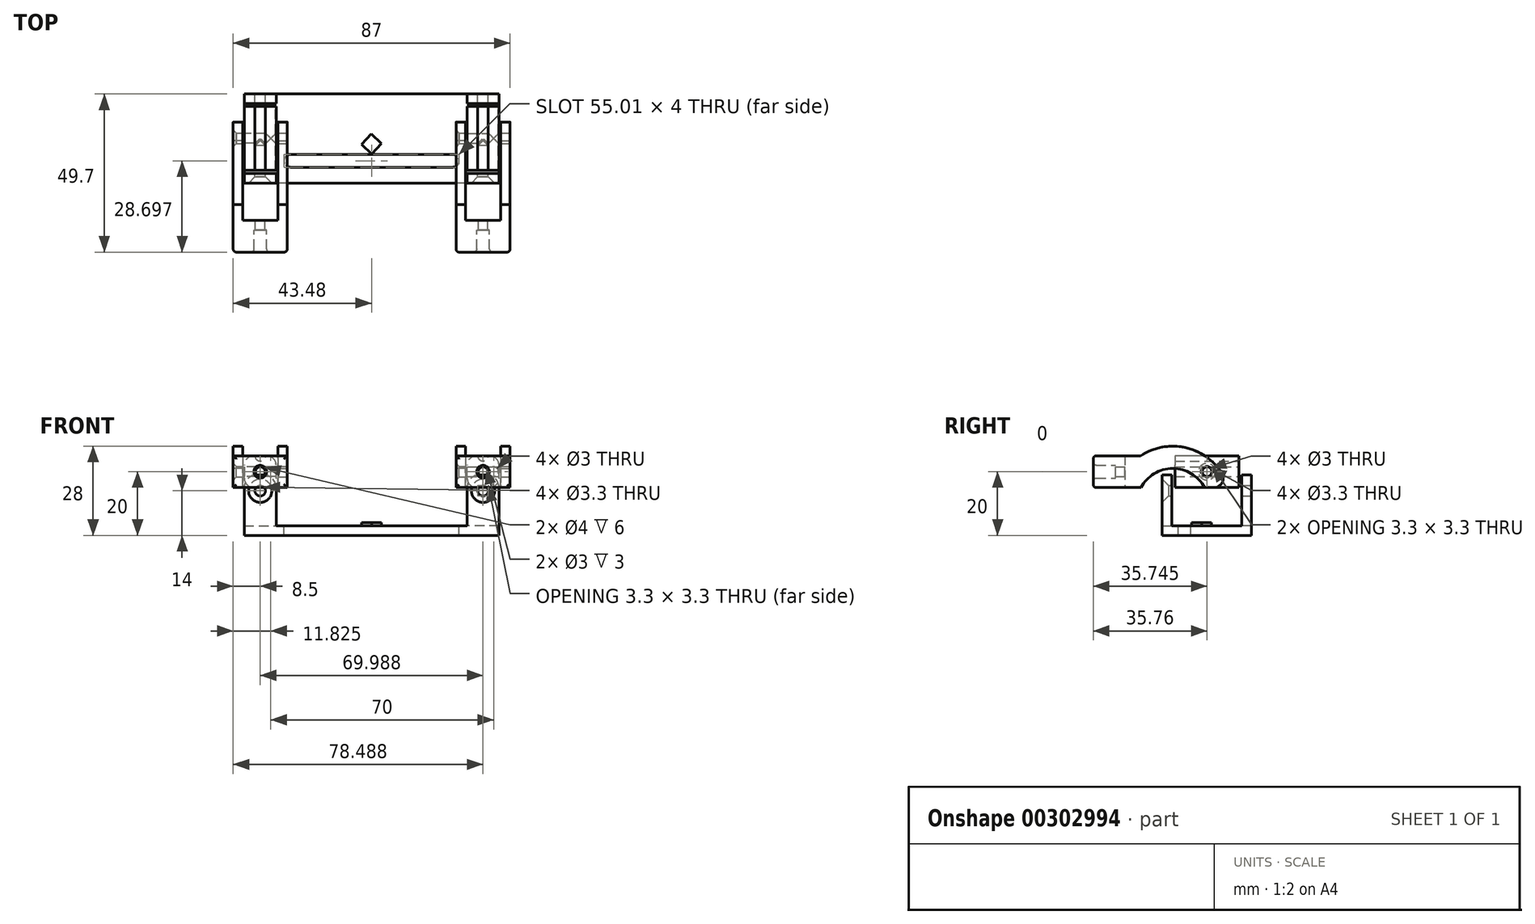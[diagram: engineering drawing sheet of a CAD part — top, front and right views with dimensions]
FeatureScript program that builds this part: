
annotation { "Feature Type Name" : "Feature", "Feature Type Description" : "" }
export const myFeature = defineFeature(function(context is Context, id is Id, definition is map)
    precondition{}
    {
        {
            var Q0;
            Q0=qCreatedBy(makeId("Front.planeOp"),FACE);
            var sketch = newSketch(context, id + "F0", { "sketchPlane" : qUnion([Q0])});
            skCircle(sketch, "E0", {"center": v(0, 0) * mm, "radius": 2 * mm});
            skCircle(sketch, "E1", {"center": v(0, 0) * mm, "radius": 1.5 * mm});
            skCircle(sketch, "E2", {"center": v(0, 0) * mm, "radius": 3.5 * mm});
            skLineSegment(sketch, "E3.bottom", {"start": v(8.5, 5) * mm, "end": v(-8.5, 5) * mm});
            skLineSegment(sketch, "E3.top", {"start": v(8.5, -5) * mm, "end": v(-8.5, -5) * mm});
            skLineSegment(sketch, "E3.left", {"start": v(8.5, 5) * mm, "end": v(8.5, -5) * mm});
            skLineSegment(sketch, "E3.right", {"start": v(-8.5, 5) * mm, "end": v(-8.5, -5) * mm});
            skSolve(sketch);
        }
        {
            var Q0;
            Q0=makeQuery(id+"F0.imprint","IMPRINT",FACE,{"disambiguationData":[TD([[makeQuery(id+"F0.imprint","IMPRINT",EDGE,{"derivedFrom":sQuery(id+"F0.wireOp",EDGE,"E0")}),-1.0]])]});
            extrude(context, id + "F1", {"entities" : qUnion([Q0]), "depth" : 10 * mm});
        }
        {
            var Q0;
            Q0=makeQuery(id+"F0.imprint","IMPRINT",FACE,{"disambiguationData":[TD([[makeQuery(id+"F0.imprint","IMPRINT",EDGE,{"derivedFrom":sQuery(id+"F0.wireOp",EDGE,"E2")}),-1.0]])]});
            extrude(context, id + "F2", {"entities" : qUnion([Q0]), "operationType" : NewBodyOperationType.ADD, "depth" : 10 * mm});
        }
        {
            var Q0;
            Q0=makeQuery(id+"F0.imprint","IMPRINT",FACE,{"disambiguationData":[TD([[makeQuery(id+"F0.imprint","IMPRINT",EDGE,{"derivedFrom":sQuery(id+"F0.wireOp",EDGE,"E0")}),1.0]])]});
            extrude(context, id + "F3", {"entities" : qUnion([Q0]), "operationType" : NewBodyOperationType.ADD, "depth" : 3 * mm});
        }
        {
            var Q0;
            {var subQ5=sQuery(id+"F0.wireOp",EDGE,"E3.left");Q0=makeQuery(id+"F0.imprint","IMPRINT",FACE,{"disambiguationData":[TD([[makeQuery(id+"F0.imprint","IMPRINT",EDGE,{"derivedFrom":subQ5}),-1.0]])]});}
            var sketch = newSketch(context, id + "F4", { "sketchPlane" : qUnion([Q0])});
            skLineSegment(sketch, "E4.bottom", {"start": v(8.5, 5) * mm, "end": v(5.5, 5) * mm});
            skLineSegment(sketch, "E4.top", {"start": v(8.5, -5) * mm, "end": v(5.5, -5) * mm});
            skLineSegment(sketch, "E4.left", {"start": v(8.5, 5) * mm, "end": v(8.5, -5) * mm});
            skLineSegment(sketch, "E4.right", {"start": v(5.5, 5) * mm, "end": v(5.5, -5) * mm});
            skSolve(sketch);
        }
        {
            var Q0;
            {var subQ1=sQuery(id+"F4.wireOp",EDGE,"E4.bottom");Q0=makeQuery(id+"F4.imprint","IMPRINT",FACE,{"disambiguationData":[TD([[makeQuery(id+"F4.imprint","IMPRINT",EDGE,{"derivedFrom":subQ1}),1.0]])]});}
            var Q1;
            {var subQ0=sQuery(id+"F4.wireOp",EDGE,"E4.right");var subQ1=sQuery(id+"F0.wireOp",EDGE,"E2");var subQ2=makeQuery(id+"F0.imprint","IMPRINT",EDGE,{"disambiguationData":[TD([[makeQuery(id+"F0.imprint","INTERSECT",VERTEX,{"derivedFrom":[subQ1,sQuery(id+"F0.wireOp",EDGE,"E3.bottom")]}),1.0]])],"derivedFrom":subQ1});var subQ3=makeQuery(id+"F4.imprint","INTERSECT",VERTEX,{"disambiguationData":[OD(0.0)],"derivedFrom":[subQ2,subQ0]});Q1=makeQuery(id+"F4.imprint","IMPRINT",FACE,{"disambiguationData":[TD([[makeQuery(id+"F4.imprint","IMPRINT",EDGE,{"disambiguationData":[TD([[subQ3,-1.0]])],"derivedFrom":subQ0}),1.0]])]});}
            extrude(context, id + "F5", {"entities" : qUnion([Q0, Q1]), "operationType" : NewBodyOperationType.ADD, "oppositeDirection" : true, "depth" : 5 * mm});
        }
        {
            var Q0;
            {var subQ0=sQuery(id+"F0.wireOp",EDGE,"E0");var subQ1=sQuery(id+"F0.wireOp",EDGE,"E3.top");var subQ2=sQuery(id+"F0.wireOp",EDGE,"E3.bottom");var subQ3=sQuery(id+"F0.wireOp",EDGE,"E2");Q0=makeQuery(id+"F3.boolean.opBoolean","MERGE",FACE,{"derivedFrom":[makeQuery(id+"F2.boolean.opBoolean","MERGE",FACE,{"derivedFrom":[makeQuery(id+"F1.opExtrude","CAP_FACE",FACE,{"disambiguationData":[OSD([subQ0,subQ3])],"isStart":true}),makeQuery(id+"F2.opExtrude","CAP_FACE",FACE,{"disambiguationData":[OSD([subQ3,subQ2,subQ1,sQuery(id+"F0.wireOp",EDGE,"E3.right")])],"isStart":true}),makeQuery(id+"F2.opExtrude","CAP_FACE",FACE,{"disambiguationData":[OSD([subQ3,subQ2,subQ1,sQuery(id+"F0.wireOp",EDGE,"E3.left")])],"isStart":true})]}),makeQuery(id+"F3.opExtrude","CAP_FACE",FACE,{"disambiguationData":[OSD([subQ0,sQuery(id+"F0.wireOp",EDGE,"E1")])],"isStart":true})]});}
            var sketch = newSketch(context, id + "F6", { "sketchPlane" : qUnion([Q0])});
            skLineSegment(sketch, "E5.bottom", {"start": v(8.5, 5) * mm, "end": v(5.5, 5) * mm});
            skLineSegment(sketch, "E5.top", {"start": v(8.5, -5) * mm, "end": v(5.5, -5) * mm});
            skLineSegment(sketch, "E5.left", {"start": v(8.5, 5) * mm, "end": v(8.5, -5) * mm});
            skLineSegment(sketch, "E5.right", {"start": v(5.5, 5) * mm, "end": v(5.5, -5) * mm});
            skSolve(sketch);
        }
        {
            var Q0;
            Q0=makeQuery(id+"F6.imprint","IMPRINT",FACE,{"disambiguationData":[TD([[makeQuery(id+"F6.imprint","IMPRINT",EDGE,{"derivedFrom":sQuery(id+"F6.wireOp",EDGE,"E5.bottom")}),-1.0]])]});
            extrude(context, id + "F7", {"entities" : qUnion([Q0]), "operationType" : NewBodyOperationType.ADD, "depth" : 5 * mm});
        }
        {
            var Q0;
            Q0=makeQuery(id+"F7.boolean.opBoolean","MERGE",FACE,{"derivedFrom":[makeQuery(id+"F2.opExtrude","SWEPT_FACE",FACE,{"disambiguationData":[OSD([sQuery(id+"F0.wireOp",EDGE,"E3.right")])]}),makeQuery(id+"F7.opExtrude","SWEPT_FACE",FACE,{"disambiguationData":[OSD([sQuery(id+"F6.wireOp",EDGE,"E5.left")])]})]});
            var sketch = newSketch(context, id + "F8", { "sketchPlane" : qUnion([Q0])});
            skLineSegment(sketch, "E6", {"start": v(0, 0) * mm, "end": v(-25.94, 0) * mm, "construction": true});
            skPoint(sketch, "E6.endSnap0", {"position": v(-5, 0) * mm});
            skLineSegment(sketch, "E7", {"start": v(0, -5) * mm, "end": v(0, 1) * mm, "construction": true});
            skLineSegment(sketch, "E8", {"start": v(0, 1) * mm, "end": v(-15, 1) * mm, "construction": true});
            skLineSegment(sketch, "E9", {"start": v(0, -5) * mm, "end": v(-25, -5) * mm, "construction": true});
            skArc(sketch, "E10", {"start": v(-15, 1) * mm, "mid": v(-20.83, -0.62) * mm, "end": v(-25, -5) * mm});
            skArc(sketch, "E11", {"start": v(-5, -5) * mm, "mid": v(-9.17, -0.62) * mm, "end": v(-15, 1) * mm});
            skArc(sketch, "E12.0", {"start": v(-15, 8) * mm, "mid": v(-25.92, 4.4) * mm, "end": v(-32.54, -5) * mm});
            skArc(sketch, "E12.1", {"start": v(-4.95, 5) * mm, "mid": v(-9.76, 7.23) * mm, "end": v(-15, 8) * mm});
            skLineSegment(sketch, "E13", {"start": v(-25, -5) * mm, "end": v(-33.46, -5) * mm, "construction": true});
            skLineSegment(sketch, "E14", {"start": v(-32.54, -5) * mm, "end": v(-25, -5) * mm});
            skSolve(sketch);
        }
        {
            var Q0;
            Q0=makeQuery(id+"F8.imprint","IMPRINT",FACE,{"disambiguationData":[TD([[makeQuery(id+"F8.imprint","IMPRINT",EDGE,{"derivedFrom":sQuery(id+"F8.wireOp",EDGE,"E10")}),-1.0]])]});
            extrude(context, id + "F9", {"entities" : qUnion([Q0]), "operationType" : NewBodyOperationType.ADD, "oppositeDirection" : true, "depth" : 3 * mm});
        }
        {
            var Q0;
            Q0=makeQuery(id+"F5.boolean.opBoolean","MERGE",FACE,{"derivedFrom":[makeQuery(id+"F2.opExtrude","SWEPT_FACE",FACE,{"disambiguationData":[OSD([sQuery(id+"F0.wireOp",EDGE,"E3.left")])]}),makeQuery(id+"F5.opExtrude","SWEPT_FACE",FACE,{"disambiguationData":[OSD([sQuery(id+"F4.wireOp",EDGE,"E4.left")])]})]});
            var sketch = newSketch(context, id + "F10", { "sketchPlane" : qUnion([Q0])});
            skLineSegment(sketch, "E15", {"start": v(0, 0) * mm, "end": v(0, -5.22) * mm, "construction": true});
            skLineSegment(sketch, "E16", {"start": v(0, -5) * mm, "end": v(25, -5) * mm, "construction": true});
            skLineSegment(sketch, "E17", {"start": v(0, 1) * mm, "end": v(15, 1) * mm, "construction": true});
            skArc(sketch, "E18", {"start": v(25, -5) * mm, "mid": v(20.83, -0.62) * mm, "end": v(15, 1) * mm});
            skArc(sketch, "E19", {"start": v(15, 1) * mm, "mid": v(9.17, -0.62) * mm, "end": v(5, -5) * mm});
            skArc(sketch, "E20.0", {"start": v(15, 8) * mm, "mid": v(9.76, 7.23) * mm, "end": v(4.95, 5) * mm});
            skArc(sketch, "E20.1", {"start": v(32.54, -5) * mm, "mid": v(25.92, 4.4) * mm, "end": v(15, 8) * mm});
            skLineSegment(sketch, "E21", {"start": v(25, -5) * mm, "end": v(32.54, -5) * mm});
            skSolve(sketch);
        }
        {
            var Q0;
            Q0=makeQuery(id+"F10.imprint","IMPRINT",FACE,{"disambiguationData":[TD([[makeQuery(id+"F10.imprint","IMPRINT",EDGE,{"derivedFrom":sQuery(id+"F10.wireOp",EDGE,"E18")}),-1.0]])]});
            extrude(context, id + "F11", {"entities" : qUnion([Q0]), "operationType" : NewBodyOperationType.ADD, "oppositeDirection" : true, "depth" : 3 * mm});
        }
        {
            var Q0;
            {var subQ0=sQuery(id+"F0.wireOp",EDGE,"E0");var subQ1=sQuery(id+"F0.wireOp",EDGE,"E2");Q0=makeQuery(id+"F3.boolean.opBoolean","MERGE",FACE,{"derivedFrom":[makeQuery(id+"F2.boolean.opBoolean","MERGE",FACE,{"derivedFrom":[makeQuery(id+"F1.opExtrude","CAP_FACE",FACE,{"disambiguationData":[OSD([subQ0,subQ1])],"isStart":true}),makeQuery(id+"F2.opExtrude","CAP_FACE",FACE,{"disambiguationData":[OSD([subQ1,sQuery(id+"F0.wireOp",EDGE,"E3.bottom"),sQuery(id+"F0.wireOp",EDGE,"E3.top"),sQuery(id+"F0.wireOp",EDGE,"E3.left"),sQuery(id+"F0.wireOp",EDGE,"E3.right")])],"isStart":true})]}),makeQuery(id+"F3.opExtrude","CAP_FACE",FACE,{"disambiguationData":[OSD([subQ0,sQuery(id+"F0.wireOp",EDGE,"E1")])],"isStart":true})]});}
            var sketch = newSketch(context, id + "F12", { "sketchPlane" : qUnion([Q0])});
            skLineSegment(sketch, "E22.bottom", {"start": v(5, -5) * mm, "end": v(-5, -5) * mm});
            skLineSegment(sketch, "E22.top", {"start": v(5, 5) * mm, "end": v(-5, 5) * mm});
            skLineSegment(sketch, "E22.left", {"start": v(5, -5) * mm, "end": v(5, 5) * mm});
            skLineSegment(sketch, "E22.right", {"start": v(-5, -5) * mm, "end": v(-5, 5) * mm});
            skPoint(sketch, "E22.middle", {"position": v(0, 0) * mm});
            skCircle(sketch, "E23", {"center": v(0, 0) * mm, "radius": 1.5 * mm});
            skSolve(sketch);
        }
        {
            var Q0;
            Q0=makeQuery(id+"F12.imprint","IMPRINT",FACE,{"disambiguationData":[TD([[makeQuery(id+"F12.imprint","IMPRINT",EDGE,{"derivedFrom":sQuery(id+"F12.wireOp",EDGE,"E22.bottom")}),1.0]])]});
            var Q1;
            Q1=makeQuery(id+"F12.imprint","IMPRINT",FACE,{"disambiguationData":[TD([[makeQuery(id+"F12.imprint","IMPRINT",EDGE,{"derivedFrom":sQuery(id+"F12.wireOp",EDGE,"E23")}),-1.0]])]});
            extrude(context, id + "F13", {"entities" : qUnion([Q0, Q1]), "depth" : 20 * mm});
        }
        {
            var Q0;
            Q0=makeQuery(id+"F13.opExtrude","SWEPT_BODY",BODY,{"disambiguationData":[OSD([sQuery(id+"F12.wireOp",EDGE,"E22.bottom"),sQuery(id+"F12.wireOp",EDGE,"E22.top"),sQuery(id+"F12.wireOp",EDGE,"E22.left"),sQuery(id+"F12.wireOp",EDGE,"E22.right")])]});
            transform(context, id + "F14", {"entities" : qUnion([Q0]), "transformType" : TransformType.TRANSLATION_3D, "dx" : 0 * mm, "dy" : 19.9 * mm, "dz" : 0 * mm, "makeCopy" : false});
        }
        {
            var Q0;
            Q0=makeQuery(id+"F13.opExtrude","SWEPT_BODY",BODY,{"disambiguationData":[OSD([sQuery(id+"F12.wireOp",EDGE,"E22.bottom"),sQuery(id+"F12.wireOp",EDGE,"E22.top"),sQuery(id+"F12.wireOp",EDGE,"E22.left"),sQuery(id+"F12.wireOp",EDGE,"E22.right")])]});
            transform(context, id + "F15", {"entities" : qUnion([Q0]), "transformType" : TransformType.TRANSLATION_3D, "dx" : 0 * mm, "dy" : -2 * mm, "dz" : 0 * mm, "makeCopy" : false});
        }
        {
            var Q0;
            Q0=makeQuery(id+"F13.opExtrude","SWEPT_BODY",BODY,{"disambiguationData":[OSD([sQuery(id+"F12.wireOp",EDGE,"E22.bottom"),sQuery(id+"F12.wireOp",EDGE,"E22.top"),sQuery(id+"F12.wireOp",EDGE,"E22.left"),sQuery(id+"F12.wireOp",EDGE,"E22.right")])]});
            transform(context, id + "F16", {"entities" : qUnion([Q0]), "transformType" : TransformType.TRANSLATION_3D, "dx" : 0 * mm, "dy" : 27.9 * mm, "dz" : 0 * mm, "makeCopy" : false});
        }
        {
            var Q0;
            Q0=makeQuery(id+"F11.opExtrude","SWEPT_EDGE",EDGE,{"disambiguationData":[OSD([sQuery(id+"F10.wireOp",EDGE,"E20.1"),sQuery(id+"F10.wireOp",EDGE,"E21")])]});
            var Q1;
            Q1=makeQuery(id+"F9.opExtrude","SWEPT_EDGE",EDGE,{"disambiguationData":[OSD([sQuery(id+"F8.wireOp",EDGE,"E12.0"),sQuery(id+"F8.wireOp",EDGE,"E14")])]});
            fillet(context, id + "F17", {"entities" : qUnion([Q0, Q1]), "radius" : 3 * mm, "tangentPropagation" : true, "allowEdgeOverflow" : false});
        }
        {
            var Q0;
            Q0=makeQuery(id+"F13.opExtrude","SWEPT_BODY",BODY,{"disambiguationData":[OSD([sQuery(id+"F12.wireOp",EDGE,"E22.bottom"),sQuery(id+"F12.wireOp",EDGE,"E22.top"),sQuery(id+"F12.wireOp",EDGE,"E22.left"),sQuery(id+"F12.wireOp",EDGE,"E22.right")])]});
            transform(context, id + "F18", {"entities" : qUnion([Q0]), "transformType" : TransformType.TRANSLATION_3D, "dx" : 0 * mm, "dy" : -27.4 * mm, "dz" : 0 * mm, "makeCopy" : false});
        }
        {
            var Q0;
            Q0=makeQuery(id+"F13.opExtrude","SWEPT_BODY",BODY,{"disambiguationData":[OSD([sQuery(id+"F12.wireOp",EDGE,"E22.bottom"),sQuery(id+"F12.wireOp",EDGE,"E22.top"),sQuery(id+"F12.wireOp",EDGE,"E22.left"),sQuery(id+"F12.wireOp",EDGE,"E22.right")])]});
            transform(context, id + "F19", {"entities" : qUnion([Q0]), "transformType" : TransformType.TRANSLATION_3D, "dx" : 0 * mm, "dy" : -2 * mm, "dz" : 0 * mm, "makeCopy" : false});
        }
        {
            var Q0;
            {var subQ0=sQuery(id+"F4.wireOp",EDGE,"E4.left");var subQ1=sQuery(id+"F0.wireOp",EDGE,"E3.left");Q0=makeQuery(id+"F11.boolean.opBoolean","MERGE",FACE,{"derivedFrom":[makeQuery(id+"F5.boolean.opBoolean","MERGE",FACE,{"derivedFrom":[makeQuery(id+"F2.opExtrude","SWEPT_FACE",FACE,{"disambiguationData":[OSD([subQ1])]}),makeQuery(id+"F5.opExtrude","SWEPT_FACE",FACE,{"disambiguationData":[OSD([subQ0])]})]}),makeQuery(id+"F11.opExtrude","CAP_FACE",FACE,{"disambiguationData":[OSD([sQuery(id+"F0.wireOp",EDGE,"E3.bottom"),subQ1,sQuery(id+"F4.wireOp",EDGE,"E4.bottom"),subQ0,sQuery(id+"F10.wireOp",EDGE,"E18"),sQuery(id+"F10.wireOp",EDGE,"E19"),sQuery(id+"F10.wireOp",EDGE,"E20.0"),sQuery(id+"F10.wireOp",EDGE,"E20.1"),sQuery(id+"F10.wireOp",EDGE,"E21")])],"isStart":true})]});}
            var sketch = newSketch(context, id + "F20", { "sketchPlane" : qUnion([Q0])});
            skCircle(sketch, "E24", {"center": v(25.74, 0) * mm, "radius": 1.65 * mm});
            skSolve(sketch);
        }
        {
            var Q0;
            Q0=makeQuery(id+"F20.imprint","IMPRINT",FACE,{"disambiguationData":[TD([[makeQuery(id+"F20.imprint","IMPRINT",EDGE,{"derivedFrom":sQuery(id+"F20.wireOp",EDGE,"E24")}),1.0]])]});
            extrude(context, id + "F21", {"entities" : qUnion([Q0]), "operationType" : NewBodyOperationType.REMOVE, "oppositeDirection" : true, "depth" : 25 * mm});
        }
        {
            var Q0;
            Q0=makeQuery(id+"F21.boolean.opBoolean","COPY",EDGE,{"derivedFrom":makeQuery(id+"F21.opExtrude","CAP_EDGE",EDGE,{"disambiguationData":[OSD([sQuery(id+"F20.wireOp",EDGE,"E24")])],"isStart":true})});
            var Q1;
            {var subQ0=sQuery(id+"F6.wireOp",EDGE,"E5.left");var subQ1=sQuery(id+"F0.wireOp",EDGE,"E3.right");Q1=makeQuery(id+"F21.boolean.opBoolean","INTERSECT",EDGE,{"derivedFrom":[makeQuery(id+"F9.boolean.opBoolean","MERGE",FACE,{"derivedFrom":[makeQuery(id+"F7.boolean.opBoolean","MERGE",FACE,{"derivedFrom":[makeQuery(id+"F2.opExtrude","SWEPT_FACE",FACE,{"disambiguationData":[OSD([subQ1])]}),makeQuery(id+"F7.opExtrude","SWEPT_FACE",FACE,{"disambiguationData":[OSD([subQ0])]})]}),makeQuery(id+"F9.opExtrude","CAP_FACE",FACE,{"disambiguationData":[OSD([sQuery(id+"F0.wireOp",EDGE,"E3.bottom"),subQ1,sQuery(id+"F6.wireOp",EDGE,"E5.bottom"),subQ0,sQuery(id+"F8.wireOp",EDGE,"E10"),sQuery(id+"F8.wireOp",EDGE,"E11"),sQuery(id+"F8.wireOp",EDGE,"E12.0"),sQuery(id+"F8.wireOp",EDGE,"E12.1"),sQuery(id+"F8.wireOp",EDGE,"E14")])],"isStart":true})]}),makeQuery(id+"F21.opExtrude","SWEPT_FACE",FACE,{"disambiguationData":[OSD([sQuery(id+"F20.wireOp",EDGE,"E24")])]})]});}
            chamfer(context, id + "F22", {"entities" : qUnion([Q0, Q1]), "width" : 1 * mm, "tangentPropagation" : true});
        }
        {
            var Q0;
            Q0=makeQuery(id+"F13.opExtrude","SWEPT_BODY",BODY,{"disambiguationData":[OSD([sQuery(id+"F12.wireOp",EDGE,"E22.bottom"),sQuery(id+"F12.wireOp",EDGE,"E22.top"),sQuery(id+"F12.wireOp",EDGE,"E22.left"),sQuery(id+"F12.wireOp",EDGE,"E22.right")])]});
            transform(context, id + "F23", {"entities" : qUnion([Q0]), "transformType" : TransformType.TRANSLATION_3D, "dx" : 0 * mm, "dy" : 33.1 * mm, "dz" : 0 * mm, "makeCopy" : false});
        }
        {
            var Q0;
            Q0=makeQuery(id+"F13.opExtrude","SWEPT_FACE",FACE,{"disambiguationData":[OSD([sQuery(id+"F12.wireOp",EDGE,"E22.right")])]});
            var sketch = newSketch(context, id + "F24", { "sketchPlane" : qUnion([Q0])});
            skCircle(sketch, "E25", {"center": v(58.84, 0) * mm, "radius": 1.5 * mm});
            skSolve(sketch);
        }
        {
            var Q0;
            Q0=makeQuery(id+"F24.imprint","IMPRINT",FACE,{"disambiguationData":[TD([[makeQuery(id+"F24.imprint","IMPRINT",EDGE,{"derivedFrom":sQuery(id+"F24.wireOp",EDGE,"E25")}),-1.0]])]});
            extrude(context, id + "F25", {"entities" : qUnion([Q0]), "operationType" : NewBodyOperationType.ADD, "oppositeDirection" : true, "depth" : 10 * mm});
        }
        {
            var Q0;
            Q0=makeQuery(id+"F13.opExtrude","SWEPT_FACE",FACE,{"disambiguationData":[OSD([sQuery(id+"F12.wireOp",EDGE,"E22.bottom")])]});
            var sketch = newSketch(context, id + "F26", { "sketchPlane" : qUnion([Q0])});
            skLineSegment(sketch, "E26.bottom", {"start": v(56.44, -45.64) * mm, "end": v(-23.56, -45.64) * mm});
            skLineSegment(sketch, "E26.top", {"start": v(56.44, -73.64) * mm, "end": v(-23.56, -73.64) * mm});
            skLineSegment(sketch, "E26.left", {"start": v(56.44, -45.64) * mm, "end": v(56.44, -73.64) * mm});
            skLineSegment(sketch, "E26.right", {"start": v(-23.56, -45.64) * mm, "end": v(-23.56, -73.64) * mm});
            skSolve(sketch);
        }
        {
            var Q0;
            {var subQ0=sQuery(id+"F12.wireOp",EDGE,"E22.bottom");Q0=makeQuery(id+"F26.imprint","IMPRINT",FACE,{"disambiguationData":[TD([[makeQuery(id+"F26.imprint","IMPRINT",EDGE,{"derivedFrom":makeQuery(id+"F13.opExtrude","CAP_EDGE",EDGE,{"disambiguationData":[OSD([subQ0])],"isStart":true})}),1.0]])]});}
            var Q1;
            Q1=makeQuery(id+"F26.imprint","IMPRINT",FACE,{"disambiguationData":[TD([[makeQuery(id+"F26.imprint","IMPRINT",EDGE,{"derivedFrom":sQuery(id+"F26.wireOp",EDGE,"E26.bottom")}),1.0]])]});
            extrude(context, id + "F27", {"entities" : qUnion([Q0, Q1]), "depth" : 3 * mm});
        }
        {
            var Q0;
            Q0=makeQuery(id+"F27.opExtrude","SWEPT_BODY",BODY,{"disambiguationData":[OSD([sQuery(id+"F26.wireOp",EDGE,"E26.bottom"),sQuery(id+"F26.wireOp",EDGE,"E26.top"),sQuery(id+"F26.wireOp",EDGE,"E26.left"),sQuery(id+"F26.wireOp",EDGE,"E26.right")])]});
            transform(context, id + "F28", {"entities" : qUnion([Q0]), "transformType" : TransformType.TRANSLATION_3D, "dx" : 18.55 * mm, "dy" : 0 * mm, "dz" : 0 * mm, "makeCopy" : false});
        }
        {
            var Q0;
            Q0=makeQuery(id+"F27.opExtrude","SWEPT_BODY",BODY,{"disambiguationData":[OSD([sQuery(id+"F26.wireOp",EDGE,"E26.bottom"),sQuery(id+"F26.wireOp",EDGE,"E26.top"),sQuery(id+"F26.wireOp",EDGE,"E26.left"),sQuery(id+"F26.wireOp",EDGE,"E26.right")])]});
            transform(context, id + "F29", {"entities" : qUnion([Q0]), "transformType" : TransformType.TRANSLATION_3D, "dx" : 0 * mm, "dy" : 0 * mm, "dz" : -1 * mm, "makeCopy" : false});
        }
        {
            var Q0;
            Q0=makeQuery(id+"F27.opExtrude","CAP_FACE",FACE,{"disambiguationData":[OSD([sQuery(id+"F26.wireOp",EDGE,"E26.bottom"),sQuery(id+"F26.wireOp",EDGE,"E26.top"),sQuery(id+"F26.wireOp",EDGE,"E26.left"),sQuery(id+"F26.wireOp",EDGE,"E26.right")])],"isStart":true});
            var sketch = newSketch(context, id + "F30", { "sketchPlane" : qUnion([Q0])});
            skLineSegment(sketch, "E27.bottom", {"start": v(-5.01, 45.64) * mm, "end": v(4.99, 45.64) * mm});
            skLineSegment(sketch, "E27.top", {"start": v(-5.01, 48.64) * mm, "end": v(4.99, 48.64) * mm});
            skLineSegment(sketch, "E27.left", {"start": v(-5.01, 45.64) * mm, "end": v(-5.01, 48.64) * mm});
            skLineSegment(sketch, "E27.right", {"start": v(4.99, 45.64) * mm, "end": v(4.99, 48.64) * mm});
            skLineSegment(sketch, "E28.bottom", {"start": v(-5.01, 73.64) * mm, "end": v(4.99, 73.64) * mm});
            skLineSegment(sketch, "E28.top", {"start": v(-5.01, 70.64) * mm, "end": v(4.99, 70.64) * mm});
            skLineSegment(sketch, "E28.left", {"start": v(-5.01, 73.64) * mm, "end": v(-5.01, 70.64) * mm});
            skLineSegment(sketch, "E28.right", {"start": v(4.99, 73.64) * mm, "end": v(4.99, 70.64) * mm});
            skLineSegment(sketch, "E29.bottom", {"start": v(74.99, 45.64) * mm, "end": v(64.99, 45.64) * mm});
            skLineSegment(sketch, "E29.top", {"start": v(74.99, 48.64) * mm, "end": v(64.99, 48.64) * mm});
            skLineSegment(sketch, "E29.left", {"start": v(74.99, 45.64) * mm, "end": v(74.99, 48.64) * mm});
            skLineSegment(sketch, "E29.right", {"start": v(64.99, 45.64) * mm, "end": v(64.99, 48.64) * mm});
            skLineSegment(sketch, "E30.bottom", {"start": v(74.99, 73.64) * mm, "end": v(64.99, 73.64) * mm});
            skLineSegment(sketch, "E30.top", {"start": v(74.99, 70.64) * mm, "end": v(64.99, 70.64) * mm});
            skLineSegment(sketch, "E30.left", {"start": v(74.99, 73.64) * mm, "end": v(74.99, 70.64) * mm});
            skLineSegment(sketch, "E30.right", {"start": v(64.99, 73.64) * mm, "end": v(64.99, 70.64) * mm});
            skSolve(sketch);
        }
        {
            var Q0;
            Q0=makeQuery(id+"F30.imprint","IMPRINT",FACE,{"disambiguationData":[TD([[makeQuery(id+"F30.imprint","IMPRINT",EDGE,{"derivedFrom":sQuery(id+"F30.wireOp",EDGE,"E29.bottom")}),-1.0]])]});
            var Q1;
            Q1=makeQuery(id+"F30.imprint","IMPRINT",FACE,{"disambiguationData":[TD([[makeQuery(id+"F30.imprint","IMPRINT",EDGE,{"derivedFrom":sQuery(id+"F30.wireOp",EDGE,"E30.bottom")}),1.0]])]});
            var Q2;
            Q2=makeQuery(id+"F30.imprint","IMPRINT",FACE,{"disambiguationData":[TD([[makeQuery(id+"F30.imprint","IMPRINT",EDGE,{"derivedFrom":sQuery(id+"F30.wireOp",EDGE,"E27.bottom")}),-1.0]])]});
            var Q3;
            Q3=makeQuery(id+"F30.imprint","IMPRINT",FACE,{"disambiguationData":[TD([[makeQuery(id+"F30.imprint","IMPRINT",EDGE,{"derivedFrom":sQuery(id+"F30.wireOp",EDGE,"E28.bottom")}),1.0]])]});
            extrude(context, id + "F31", {"entities" : qUnion([Q0, Q1, Q2, Q3]), "operationType" : NewBodyOperationType.ADD, "depth" : 16 * mm});
        }
        {
            var Q0;
            Q0=makeQuery(id+"F31.boolean.opBoolean","MERGE",FACE,{"derivedFrom":[makeQuery(id+"F27.opExtrude","SWEPT_FACE",FACE,{"disambiguationData":[OSD([sQuery(id+"F26.wireOp",EDGE,"E26.top")])]}),makeQuery(id+"F31.opExtrude","SWEPT_FACE",FACE,{"disambiguationData":[OSD([sQuery(id+"F30.wireOp",EDGE,"E28.bottom")])]}),makeQuery(id+"F31.opExtrude","SWEPT_FACE",FACE,{"disambiguationData":[OSD([sQuery(id+"F30.wireOp",EDGE,"E30.bottom")])]})]});
            var sketch = newSketch(context, id + "F32", { "sketchPlane" : qUnion([Q0])});
            skCircle(sketch, "E31", {"center": v(0, 5) * mm, "radius": 1.65 * mm});
            skLineSegment(sketch, "E32", {"start": v(-64.99, 5) * mm, "end": v(-69.99, 5) * mm, "construction": true});
            skCircle(sketch, "E33", {"center": v(-69.99, 5) * mm, "radius": 1.65 * mm});
            skLineSegment(sketch, "E34", {"start": v(-69.99, 10) * mm, "end": v(-69.99, 5) * mm, "construction": true});
            skLineSegment(sketch, "E35", {"start": v(0.01, 10) * mm, "end": v(0.01, 5) * mm, "construction": true});
            skSolve(sketch);
        }
        {
            var Q0;
            Q0=makeQuery(id+"F32.imprint","IMPRINT",FACE,{"disambiguationData":[TD([[makeQuery(id+"F32.imprint","IMPRINT",EDGE,{"derivedFrom":sQuery(id+"F32.wireOp",EDGE,"E33")}),1.0]])]});
            var Q1;
            Q1=makeQuery(id+"F32.imprint","IMPRINT",FACE,{"disambiguationData":[TD([[makeQuery(id+"F32.imprint","IMPRINT",EDGE,{"derivedFrom":sQuery(id+"F32.wireOp",EDGE,"E31")}),1.0]])]});
            extrude(context, id + "F33", {"entities" : qUnion([Q0, Q1]), "operationType" : NewBodyOperationType.REMOVE, "oppositeDirection" : true, "depth" : 30 * mm});
        }
        {
            var Q0;
            Q0=makeQuery(id+"F33.boolean.opBoolean","COPY",EDGE,{"derivedFrom":makeQuery(id+"F33.opExtrude","CAP_EDGE",EDGE,{"disambiguationData":[OSD([sQuery(id+"F32.wireOp",EDGE,"E33")])],"isStart":true})});
            var Q1;
            Q1=makeQuery(id+"F33.boolean.opBoolean","COPY",EDGE,{"derivedFrom":makeQuery(id+"F33.opExtrude","CAP_EDGE",EDGE,{"disambiguationData":[OSD([sQuery(id+"F32.wireOp",EDGE,"E31")])],"isStart":true})});
            var Q2;
            Q2=makeQuery(id+"F33.boolean.opBoolean","INTERSECT",EDGE,{"derivedFrom":[makeQuery(id+"F31.boolean.opBoolean","MERGE",FACE,{"derivedFrom":[makeQuery(id+"F27.opExtrude","SWEPT_FACE",FACE,{"disambiguationData":[OSD([sQuery(id+"F26.wireOp",EDGE,"E26.bottom")])]}),makeQuery(id+"F31.opExtrude","SWEPT_FACE",FACE,{"disambiguationData":[OSD([sQuery(id+"F30.wireOp",EDGE,"E27.bottom")])]}),makeQuery(id+"F31.opExtrude","SWEPT_FACE",FACE,{"disambiguationData":[OSD([sQuery(id+"F30.wireOp",EDGE,"E29.bottom")])]})]}),makeQuery(id+"F33.opExtrude","SWEPT_FACE",FACE,{"disambiguationData":[OSD([sQuery(id+"F32.wireOp",EDGE,"E33")])]})]});
            var Q3;
            Q3=makeQuery(id+"F33.boolean.opBoolean","INTERSECT",EDGE,{"derivedFrom":[makeQuery(id+"F31.boolean.opBoolean","MERGE",FACE,{"derivedFrom":[makeQuery(id+"F27.opExtrude","SWEPT_FACE",FACE,{"disambiguationData":[OSD([sQuery(id+"F26.wireOp",EDGE,"E26.bottom")])]}),makeQuery(id+"F31.opExtrude","SWEPT_FACE",FACE,{"disambiguationData":[OSD([sQuery(id+"F30.wireOp",EDGE,"E27.bottom")])]}),makeQuery(id+"F31.opExtrude","SWEPT_FACE",FACE,{"disambiguationData":[OSD([sQuery(id+"F30.wireOp",EDGE,"E29.bottom")])]})]}),makeQuery(id+"F33.opExtrude","SWEPT_FACE",FACE,{"disambiguationData":[OSD([sQuery(id+"F32.wireOp",EDGE,"E31")])]})]});
            chamfer(context, id + "F34", {"entities" : qUnion([Q0, Q1, Q2, Q3]), "width" : 2 * mm, "tangentPropagation" : true});
        }
        {
            var Q0;
            Q0=makeQuery(id+"F31.opExtrude","CAP_EDGE",EDGE,{"disambiguationData":[OSD([sQuery(id+"F30.wireOp",EDGE,"E28.left")])],"isStart":false});
            var Q1;
            Q1=makeQuery(id+"F31.opExtrude","CAP_EDGE",EDGE,{"disambiguationData":[OSD([sQuery(id+"F30.wireOp",EDGE,"E28.right")])],"isStart":false});
            var Q2;
            Q2=makeQuery(id+"F31.opExtrude","CAP_EDGE",EDGE,{"disambiguationData":[OSD([sQuery(id+"F30.wireOp",EDGE,"E27.right")])],"isStart":false});
            var Q3;
            Q3=makeQuery(id+"F31.opExtrude","CAP_EDGE",EDGE,{"disambiguationData":[OSD([sQuery(id+"F30.wireOp",EDGE,"E27.left")])],"isStart":false});
            var Q4;
            Q4=makeQuery(id+"F31.opExtrude","CAP_EDGE",EDGE,{"disambiguationData":[OSD([sQuery(id+"F30.wireOp",EDGE,"E30.left")])],"isStart":false});
            var Q5;
            Q5=makeQuery(id+"F31.opExtrude","CAP_EDGE",EDGE,{"disambiguationData":[OSD([sQuery(id+"F30.wireOp",EDGE,"E29.left")])],"isStart":false});
            var Q6;
            Q6=makeQuery(id+"F31.opExtrude","CAP_EDGE",EDGE,{"disambiguationData":[OSD([sQuery(id+"F30.wireOp",EDGE,"E29.right")])],"isStart":false});
            var Q7;
            Q7=makeQuery(id+"F31.opExtrude","CAP_EDGE",EDGE,{"disambiguationData":[OSD([sQuery(id+"F30.wireOp",EDGE,"E30.right")])],"isStart":false});
            fillet(context, id + "F35", {"entities" : qUnion([Q0, Q1, Q2, Q3, Q4, Q5, Q6, Q7]), "radius" : 4 * mm, "tangentPropagation" : true, "allowEdgeOverflow" : false});
        }
        {
            var Q0;
            Q0=makeQuery(id+"F13.opExtrude","SWEPT_BODY",BODY,{"disambiguationData":[OSD([sQuery(id+"F12.wireOp",EDGE,"E22.bottom"),sQuery(id+"F12.wireOp",EDGE,"E22.top"),sQuery(id+"F12.wireOp",EDGE,"E22.left"),sQuery(id+"F12.wireOp",EDGE,"E22.right")])]});
            transform(context, id + "F36", {"entities" : qUnion([Q0]), "transformType" : TransformType.TRANSLATION_3D, "dx" : 0 * mm, "dy" : 32.8 * mm, "dz" : 0 * mm, "makeCopy" : false});
        }
        {
            var Q0;
            Q0=makeQuery(id+"F13.opExtrude","CAP_FACE",FACE,{"disambiguationData":[OSD([sQuery(id+"F12.wireOp",EDGE,"E22.bottom"),sQuery(id+"F12.wireOp",EDGE,"E22.top"),sQuery(id+"F12.wireOp",EDGE,"E22.left"),sQuery(id+"F12.wireOp",EDGE,"E22.right")])],"isStart":false});
            var sketch = newSketch(context, id + "F37", { "sketchPlane" : qUnion([Q0])});
            skCircle(sketch, "E36", {"center": v(0, 0) * mm, "radius": 1.5 * mm});
            skSolve(sketch);
        }
        {
            var Q0;
            Q0=makeQuery(id+"F37.imprint","IMPRINT",FACE,{"disambiguationData":[TD([[makeQuery(id+"F37.imprint","IMPRINT",EDGE,{"derivedFrom":sQuery(id+"F37.wireOp",EDGE,"E36")}),-1.0]])]});
            extrude(context, id + "F38", {"entities" : qUnion([Q0]), "operationType" : NewBodyOperationType.ADD, "oppositeDirection" : true, "depth" : 20 * mm});
        }
        {
            var Q0;
            Q0=makeQuery(id+"F27.opExtrude","CAP_FACE",FACE,{"disambiguationData":[OSD([sQuery(id+"F26.wireOp",EDGE,"E26.bottom"),sQuery(id+"F26.wireOp",EDGE,"E26.top"),sQuery(id+"F26.wireOp",EDGE,"E26.left"),sQuery(id+"F26.wireOp",EDGE,"E26.right")])],"isStart":true});
            var sketch = newSketch(context, id + "F39", { "sketchPlane" : qUnion([Q0])});
            skLineSegment(sketch, "E37", {"start": v(34.99, 45.64) * mm, "end": v(34.99, 50.64) * mm, "construction": true});
            skLineSegment(sketch, "E38", {"start": v(62.49, 50.64) * mm, "end": v(7.49, 50.64) * mm, "construction": true});
            skLineSegment(sketch, "E39.bottom", {"start": v(62.49, 50.64) * mm, "end": v(7.47, 50.64) * mm});
            skLineSegment(sketch, "E39.top", {"start": v(62.49, 54.64) * mm, "end": v(7.47, 54.64) * mm});
            skLineSegment(sketch, "E39.left", {"start": v(62.49, 50.64) * mm, "end": v(62.49, 54.64) * mm});
            skLineSegment(sketch, "E39.right", {"start": v(7.47, 50.64) * mm, "end": v(7.47, 54.64) * mm});
            skSolve(sketch);
        }
        {
            var Q0;
            Q0=makeQuery(id+"F39.imprint","IMPRINT",FACE,{"disambiguationData":[TD([[makeQuery(id+"F39.imprint","IMPRINT",EDGE,{"derivedFrom":sQuery(id+"F39.wireOp",EDGE,"E39.bottom")}),-1.0]])]});
            extrude(context, id + "F40", {"entities" : qUnion([Q0]), "operationType" : NewBodyOperationType.REMOVE, "oppositeDirection" : true, "depth" : 5 * mm});
        }
        {
            var Q0;
            Q0=makeQuery(id+"F40.boolean.opBoolean","COPY",EDGE,{"derivedFrom":makeQuery(id+"F40.opExtrude","SWEPT_EDGE",EDGE,{"disambiguationData":[OSD([sQuery(id+"F39.wireOp",EDGE,"E39.bottom"),sQuery(id+"F39.wireOp",EDGE,"E39.left")])]})});
            var Q1;
            Q1=makeQuery(id+"F40.boolean.opBoolean","COPY",EDGE,{"derivedFrom":makeQuery(id+"F40.opExtrude","SWEPT_EDGE",EDGE,{"disambiguationData":[OSD([sQuery(id+"F39.wireOp",EDGE,"E39.top"),sQuery(id+"F39.wireOp",EDGE,"E39.left")])]})});
            var Q2;
            Q2=makeQuery(id+"F40.boolean.opBoolean","COPY",EDGE,{"derivedFrom":makeQuery(id+"F40.opExtrude","SWEPT_EDGE",EDGE,{"disambiguationData":[OSD([sQuery(id+"F39.wireOp",EDGE,"E39.top"),sQuery(id+"F39.wireOp",EDGE,"E39.right")])]})});
            var Q3;
            Q3=makeQuery(id+"F40.boolean.opBoolean","COPY",EDGE,{"derivedFrom":makeQuery(id+"F40.opExtrude","SWEPT_EDGE",EDGE,{"disambiguationData":[OSD([sQuery(id+"F39.wireOp",EDGE,"E39.bottom"),sQuery(id+"F39.wireOp",EDGE,"E39.right")])]})});
            fillet(context, id + "F41", {"entities" : qUnion([Q0, Q1, Q2, Q3]), "radius" : 2 * mm, "tangentPropagation" : true, "allowEdgeOverflow" : false});
        }
        {
            var Q0;
            Q0=makeQuery(id+"F13.opExtrude","SWEPT_BODY",BODY,{"disambiguationData":[OSD([sQuery(id+"F12.wireOp",EDGE,"E22.bottom"),sQuery(id+"F12.wireOp",EDGE,"E22.top"),sQuery(id+"F12.wireOp",EDGE,"E22.left"),sQuery(id+"F12.wireOp",EDGE,"E22.right")])]});
            transform(context, id + "F42", {"entities" : qUnion([Q0]), "transformType" : TransformType.TRANSLATION_3D, "dx" : 0 * mm, "dy" : -32.6 * mm, "dz" : 0 * mm, "makeCopy" : false});
        }
        {
            var Q0;
            Q0=makeQuery(id+"F1.opExtrude","SWEPT_BODY",BODY,{"disambiguationData":[OSD([sQuery(id+"F0.wireOp",EDGE,"E0"),sQuery(id+"F0.wireOp",EDGE,"E2")])]});
            transform(context, id + "F43", {"entities" : qUnion([Q0]), "transformType" : TransformType.TRANSLATION_3D, "dx" : 0 * mm, "dy" : 33.4 * mm, "dz" : 0 * mm, "makeCopy" : false});
        }
        {
            var Q0;
            Q0=makeQuery(id+"F1.opExtrude","SWEPT_BODY",BODY,{"disambiguationData":[OSD([sQuery(id+"F0.wireOp",EDGE,"E0"),sQuery(id+"F0.wireOp",EDGE,"E2")])]});
            transform(context, id + "F44", {"entities" : qUnion([Q0]), "transformType" : TransformType.TRANSLATION_3D, "dx" : 0 * mm, "dy" : -0.26 * mm, "dz" : 0 * mm, "makeCopy" : false});
        }
        {
            var Q0;
            Q0=makeQuery(id+"F13.opExtrude","SWEPT_BODY",BODY,{"disambiguationData":[OSD([sQuery(id+"F12.wireOp",EDGE,"E22.bottom"),sQuery(id+"F12.wireOp",EDGE,"E22.top"),sQuery(id+"F12.wireOp",EDGE,"E22.left"),sQuery(id+"F12.wireOp",EDGE,"E22.right")])]});
            transform(context, id + "F45", {"entities" : qUnion([Q0]), "transformType" : TransformType.TRANSLATION_3D, "dx" : 70 * mm, "dy" : 0 * mm, "dz" : 0 * mm, "makeCopy" : true});
        }
        {
            var Q0;
            Q0=makeQuery(id+"F1.opExtrude","SWEPT_BODY",BODY,{"disambiguationData":[OSD([sQuery(id+"F0.wireOp",EDGE,"E0"),sQuery(id+"F0.wireOp",EDGE,"E2")])]});
            transform(context, id + "F46", {"entities" : qUnion([Q0]), "transformType" : TransformType.TRANSLATION_3D, "dx" : 70 * mm, "dy" : 0 * mm, "dz" : 0 * mm, "makeCopy" : true});
        }
        {
            var Q0;
            Q0=makeQuery(id+"F27.opExtrude","CAP_FACE",FACE,{"disambiguationData":[OSD([sQuery(id+"F26.wireOp",EDGE,"E26.bottom"),sQuery(id+"F26.wireOp",EDGE,"E26.top"),sQuery(id+"F26.wireOp",EDGE,"E26.left"),sQuery(id+"F26.wireOp",EDGE,"E26.right")])],"isStart":true});
            var sketch = newSketch(context, id + "F47", { "sketchPlane" : qUnion([Q0])});
            skCircle(sketch, "E40.cCircle", {"center": v(34.98, 57.93) * mm, "radius": 2.21 * mm, "construction": true});
            skPoint(sketch, "E40.cCircle.centerSnap0", {"position": v(34.98, 54.64) * mm});
            skLineSegment(sketch, "E40.0", {"start": v(31.85, 57.85) * mm, "end": v(34.9, 61.06) * mm});
            skLineSegment(sketch, "E40.1", {"start": v(34.9, 61.06) * mm, "end": v(38.11, 58.01) * mm});
            skLineSegment(sketch, "E40.2", {"start": v(38.11, 58.01) * mm, "end": v(35.06, 54.8) * mm});
            skLineSegment(sketch, "E40.3", {"start": v(35.06, 54.8) * mm, "end": v(31.85, 57.85) * mm});
            skPoint(sketch, "E40.0.midPoint", {"position": v(33.38, 59.46) * mm});
            skSolve(sketch);
        }
        {
            var Q0;
            Q0=makeQuery(id+"F47.imprint","IMPRINT",FACE,{"disambiguationData":[TD([[makeQuery(id+"F47.imprint","IMPRINT",EDGE,{"derivedFrom":sQuery(id+"F47.wireOp",EDGE,"E40.0")}),-1.0]])]});
            extrude(context, id + "F48", {"entities" : qUnion([Q0]), "operationType" : NewBodyOperationType.ADD, "depth" : 1 * mm});
        }
        {
            var Q0;
            Q0=makeQuery(id+"F13.opExtrude","SWEPT_BODY",BODY,{"disambiguationData":[OSD([sQuery(id+"F12.wireOp",EDGE,"E22.bottom"),sQuery(id+"F12.wireOp",EDGE,"E22.top"),sQuery(id+"F12.wireOp",EDGE,"E22.left"),sQuery(id+"F12.wireOp",EDGE,"E22.right")])]});
            var Q1;
            Q1=makeQuery(id+"F45.opPattern","COPY",BODY,{"derivedFrom":makeQuery(id+"F13.opExtrude","SWEPT_BODY",BODY,{"disambiguationData":[OSD([sQuery(id+"F12.wireOp",EDGE,"E22.bottom"),sQuery(id+"F12.wireOp",EDGE,"E22.top"),sQuery(id+"F12.wireOp",EDGE,"E22.left"),sQuery(id+"F12.wireOp",EDGE,"E22.right")])]}),"instanceName":"1"});
            transform(context, id + "F49", {"entities" : qUnion([Q0, Q1]), "transformType" : TransformType.TRANSLATION_3D, "dx" : 0 * mm, "dy" : 0 * mm, "dz" : 30 * mm, "makeCopy" : false});
        }
        {
            var Q0;
            Q0=makeQuery(id+"F45.opPattern","COPY",FACE,{"derivedFrom":makeQuery(id+"F13.opExtrude","CAP_FACE",FACE,{"disambiguationData":[OSD([sQuery(id+"F12.wireOp",EDGE,"E22.bottom"),sQuery(id+"F12.wireOp",EDGE,"E22.top"),sQuery(id+"F12.wireOp",EDGE,"E22.left"),sQuery(id+"F12.wireOp",EDGE,"E22.right")])],"isStart":false}),"instanceName":"1"});
            var sketch = newSketch(context, id + "F50", { "sketchPlane" : qUnion([Q0])});
            skCircle(sketch, "E41", {"center": v(-73.33, 30) * mm, "radius": 1.5 * mm});
            skPoint(sketch, "E41.centerSnap0", {"position": v(-75, 30) * mm});
            skPoint(sketch, "E41.centerSnap1", {"position": v(-73.33, 35) * mm});
            skSolve(sketch);
        }
        {
            var Q0;
            Q0=makeQuery(id+"F50.imprint","IMPRINT",FACE,{"disambiguationData":[TD([[makeQuery(id+"F50.imprint","IMPRINT",EDGE,{"derivedFrom":sQuery(id+"F50.wireOp",EDGE,"E41")}),1.0]])]});
            extrude(context, id + "F51", {"entities" : qUnion([Q0]), "operationType" : NewBodyOperationType.REMOVE, "oppositeDirection" : true, "depth" : 25 * mm});
        }
        {
            var Q0;
            Q0=makeQuery(id+"F13.opExtrude","CAP_FACE",FACE,{"disambiguationData":[OSD([sQuery(id+"F12.wireOp",EDGE,"E22.bottom"),sQuery(id+"F12.wireOp",EDGE,"E22.top"),sQuery(id+"F12.wireOp",EDGE,"E22.left"),sQuery(id+"F12.wireOp",EDGE,"E22.right")])],"isStart":false});
            var sketch = newSketch(context, id + "F52", { "sketchPlane" : qUnion([Q0])});
            skCircle(sketch, "E42", {"center": v(-3.32, 30) * mm, "radius": 1.5 * mm});
            skPoint(sketch, "E42.centerSnap0", {"position": v(-5, 30) * mm});
            skPoint(sketch, "E42.centerSnap1", {"position": v(-3.32, 35) * mm});
            skSolve(sketch);
        }
        {
            var Q0;
            Q0=makeQuery(id+"F52.imprint","IMPRINT",FACE,{"disambiguationData":[TD([[makeQuery(id+"F52.imprint","IMPRINT",EDGE,{"derivedFrom":sQuery(id+"F52.wireOp",EDGE,"E42")}),1.0]])]});
            extrude(context, id + "F53", {"entities" : qUnion([Q0]), "operationType" : NewBodyOperationType.REMOVE, "oppositeDirection" : true, "depth" : 25 * mm});
        }
        {
            var Q0;
            {var subQ0=sQuery(id+"F12.wireOp",EDGE,"E22.left");Q0=makeQuery(id+"F38.boolean.opBoolean","MERGE",FACE,{"derivedFrom":[makeQuery(id+"F25.boolean.opBoolean","MERGE",FACE,{"derivedFrom":[makeQuery(id+"F13.opExtrude","SWEPT_FACE",FACE,{"disambiguationData":[OSD([subQ0])]}),makeQuery(id+"F25.opExtrude","CAP_FACE",FACE,{"disambiguationData":[OSD([sQuery(id+"F12.wireOp",EDGE,"E22.right"),sQuery(id+"F20.wireOp",EDGE,"E24"),sQuery(id+"F24.wireOp",EDGE,"E25")])],"isStart":false})]}),makeQuery(id+"F38.opExtrude","SWEPT_FACE",FACE,{"disambiguationData":[OSD([subQ0])]})]});}
            var sketch = newSketch(context, id + "F54", { "sketchPlane" : qUnion([Q0])});
            skCircle(sketch, "E43", {"center": v(-59.7, 30) * mm, "radius": 1.5 * mm});
            skPoint(sketch, "E43.centerSnap0", {"position": v(-69.7, 30) * mm});
            skPoint(sketch, "E43.centerSnap1", {"position": v(-59.7, 35) * mm});
            skSolve(sketch);
        }
        {
            var Q0;
            Q0=makeQuery(id+"F54.imprint","IMPRINT",FACE,{"disambiguationData":[TD([[makeQuery(id+"F54.imprint","IMPRINT",EDGE,{"derivedFrom":sQuery(id+"F54.wireOp",EDGE,"E43")}),1.0]])]});
            extrude(context, id + "F55", {"entities" : qUnion([Q0]), "operationType" : NewBodyOperationType.REMOVE, "oppositeDirection" : true, "depth" : 25 * mm});
        }
        {
            var Q0;
            {var subQ0=sQuery(id+"F12.wireOp",EDGE,"E22.right");Q0=makeQuery(id+"F45.opPattern","COPY",FACE,{"derivedFrom":makeQuery(id+"F38.boolean.opBoolean","MERGE",FACE,{"derivedFrom":[makeQuery(id+"F25.boolean.opBoolean","MERGE",FACE,{"derivedFrom":[makeQuery(id+"F13.opExtrude","SWEPT_FACE",FACE,{"disambiguationData":[OSD([subQ0])]}),makeQuery(id+"F25.opExtrude","CAP_FACE",FACE,{"disambiguationData":[OSD([subQ0,sQuery(id+"F20.wireOp",EDGE,"E24"),sQuery(id+"F24.wireOp",EDGE,"E25")])],"isStart":true})]}),makeQuery(id+"F38.opExtrude","SWEPT_FACE",FACE,{"disambiguationData":[OSD([subQ0])]})]}),"instanceName":"1"});}
            var sketch = newSketch(context, id + "F56", { "sketchPlane" : qUnion([Q0])});
            skCircle(sketch, "E44", {"center": v(59.7, 30) * mm, "radius": 1.5 * mm});
            skPoint(sketch, "E44.centerSnap0", {"position": v(59.7, 35) * mm});
            skPoint(sketch, "E44.centerSnap1", {"position": v(69.7, 30) * mm});
            skSolve(sketch);
        }
        {
            var Q0;
            Q0=makeQuery(id+"F56.imprint","IMPRINT",FACE,{"disambiguationData":[TD([[makeQuery(id+"F56.imprint","IMPRINT",EDGE,{"derivedFrom":sQuery(id+"F56.wireOp",EDGE,"E44")}),1.0]])]});
            extrude(context, id + "F57", {"entities" : qUnion([Q0]), "operationType" : NewBodyOperationType.REMOVE, "oppositeDirection" : true, "depth" : 25 * mm});
        }
        {
            var Q0;
            Q0=makeQuery(id+"F13.opExtrude","SWEPT_EDGE",EDGE,{"disambiguationData":[OSD([sQuery(id+"F0.wireOp",EDGE,"E3.top"),sQuery(id+"F12.wireOp",EDGE,"E22.bottom"),sQuery(id+"F12.wireOp",EDGE,"E22.left")])]});
            var Q1;
            Q1=makeQuery(id+"F13.opExtrude","SWEPT_EDGE",EDGE,{"disambiguationData":[OSD([sQuery(id+"F0.wireOp",EDGE,"E3.bottom"),sQuery(id+"F12.wireOp",EDGE,"E22.top"),sQuery(id+"F12.wireOp",EDGE,"E22.left")])]});
            var Q2;
            Q2=makeQuery(id+"F13.opExtrude","SWEPT_EDGE",EDGE,{"disambiguationData":[OSD([sQuery(id+"F0.wireOp",EDGE,"E3.bottom"),sQuery(id+"F12.wireOp",EDGE,"E22.top"),sQuery(id+"F12.wireOp",EDGE,"E22.right")])]});
            var Q3;
            Q3=makeQuery(id+"F13.opExtrude","SWEPT_EDGE",EDGE,{"disambiguationData":[OSD([sQuery(id+"F0.wireOp",EDGE,"E3.top"),sQuery(id+"F12.wireOp",EDGE,"E22.bottom"),sQuery(id+"F12.wireOp",EDGE,"E22.right")])]});
            var Q4;
            Q4=makeQuery(id+"F45.opPattern","COPY",EDGE,{"derivedFrom":makeQuery(id+"F13.opExtrude","SWEPT_EDGE",EDGE,{"disambiguationData":[OSD([sQuery(id+"F0.wireOp",EDGE,"E3.top"),sQuery(id+"F12.wireOp",EDGE,"E22.bottom"),sQuery(id+"F12.wireOp",EDGE,"E22.right")])]}),"instanceName":"1"});
            var Q5;
            Q5=makeQuery(id+"F45.opPattern","COPY",EDGE,{"derivedFrom":makeQuery(id+"F13.opExtrude","SWEPT_EDGE",EDGE,{"disambiguationData":[OSD([sQuery(id+"F0.wireOp",EDGE,"E3.bottom"),sQuery(id+"F12.wireOp",EDGE,"E22.top"),sQuery(id+"F12.wireOp",EDGE,"E22.right")])]}),"instanceName":"1"});
            var Q6;
            Q6=makeQuery(id+"F45.opPattern","COPY",EDGE,{"derivedFrom":makeQuery(id+"F13.opExtrude","SWEPT_EDGE",EDGE,{"disambiguationData":[OSD([sQuery(id+"F0.wireOp",EDGE,"E3.bottom"),sQuery(id+"F12.wireOp",EDGE,"E22.top"),sQuery(id+"F12.wireOp",EDGE,"E22.left")])]}),"instanceName":"1"});
            var Q7;
            Q7=makeQuery(id+"F45.opPattern","COPY",EDGE,{"derivedFrom":makeQuery(id+"F13.opExtrude","SWEPT_EDGE",EDGE,{"disambiguationData":[OSD([sQuery(id+"F0.wireOp",EDGE,"E3.top"),sQuery(id+"F12.wireOp",EDGE,"E22.bottom"),sQuery(id+"F12.wireOp",EDGE,"E22.left")])]}),"instanceName":"1"});
            fillet(context, id + "F58", {"entities" : qUnion([Q0, Q1, Q2, Q3, Q4, Q5, Q6, Q7]), "radius" : 3 * mm, "tangentPropagation" : true, "allowEdgeOverflow" : false});
        }
        {
            var Q0;
            Q0=makeQuery(id+"F13.opExtrude","SWEPT_BODY",BODY,{"disambiguationData":[OSD([sQuery(id+"F12.wireOp",EDGE,"E22.bottom"),sQuery(id+"F12.wireOp",EDGE,"E22.top"),sQuery(id+"F12.wireOp",EDGE,"E22.left"),sQuery(id+"F12.wireOp",EDGE,"E22.right")])]});
            var Q1;
            Q1=makeQuery(id+"F45.opPattern","COPY",BODY,{"derivedFrom":makeQuery(id+"F13.opExtrude","SWEPT_BODY",BODY,{"disambiguationData":[OSD([sQuery(id+"F12.wireOp",EDGE,"E22.bottom"),sQuery(id+"F12.wireOp",EDGE,"E22.top"),sQuery(id+"F12.wireOp",EDGE,"E22.left"),sQuery(id+"F12.wireOp",EDGE,"E22.right")])]}),"instanceName":"1"});
            transform(context, id + "F59", {"entities" : qUnion([Q0, Q1]), "transformType" : TransformType.TRANSLATION_3D, "dx" : 0 * mm, "dy" : 0 * mm, "dz" : -19 * mm, "makeCopy" : false});
        }
        {
            var Q0;
            Q0=makeQuery(id+"F46.opPattern","COPY",BODY,{"derivedFrom":makeQuery(id+"F1.opExtrude","SWEPT_BODY",BODY,{"disambiguationData":[OSD([sQuery(id+"F0.wireOp",EDGE,"E0"),sQuery(id+"F0.wireOp",EDGE,"E2")])]}),"instanceName":"1"});
            var Q1;
            Q1=makeQuery(id+"F1.opExtrude","SWEPT_BODY",BODY,{"disambiguationData":[OSD([sQuery(id+"F0.wireOp",EDGE,"E0"),sQuery(id+"F0.wireOp",EDGE,"E2")])]});
            transform(context, id + "F60", {"entities" : qUnion([Q0, Q1]), "transformType" : TransformType.TRANSLATION_3D, "dx" : 0 * mm, "dy" : 0 * mm, "dz" : 11 * mm, "makeCopy" : false});
        }
        {
            var Q0;
            Q0=makeQuery(id+"F1.opExtrude","CAP_EDGE",EDGE,{"disambiguationData":[OSD([sQuery(id+"F0.wireOp",EDGE,"E0")])],"isStart":false});
            var Q1;
            Q1=makeQuery(id+"F46.opPattern","COPY",EDGE,{"derivedFrom":makeQuery(id+"F1.opExtrude","CAP_EDGE",EDGE,{"disambiguationData":[OSD([sQuery(id+"F0.wireOp",EDGE,"E0")])],"isStart":false}),"instanceName":"1"});
            var Q2;
            Q2=makeQuery(id+"F46.opPattern","COPY",EDGE,{"derivedFrom":makeQuery(id+"F2.opExtrude","CAP_EDGE",EDGE,{"disambiguationData":[OSD([sQuery(id+"F0.wireOp",EDGE,"E3.right")])],"isStart":false}),"instanceName":"1"});
            var Q3;
            Q3=makeQuery(id+"F46.opPattern","COPY",EDGE,{"derivedFrom":makeQuery(id+"F2.opExtrude","CAP_EDGE",EDGE,{"disambiguationData":[OSD([sQuery(id+"F0.wireOp",EDGE,"E3.left")])],"isStart":false}),"instanceName":"1"});
            var Q4;
            Q4=makeQuery(id+"F46.opPattern","COPY",EDGE,{"derivedFrom":makeQuery(id+"F2.opExtrude","CAP_EDGE",EDGE,{"disambiguationData":[OSD([sQuery(id+"F0.wireOp",EDGE,"E3.bottom")])],"isStart":false}),"instanceName":"1"});
            var Q5;
            Q5=makeQuery(id+"F46.opPattern","COPY",EDGE,{"derivedFrom":makeQuery(id+"F2.opExtrude","CAP_EDGE",EDGE,{"disambiguationData":[OSD([sQuery(id+"F0.wireOp",EDGE,"E3.top")])],"isStart":false}),"instanceName":"1"});
            var Q6;
            {var subQ0=sQuery(id+"F0.wireOp",EDGE,"E2");Q6=makeQuery(id+"F2.boolean.opBoolean","MERGE",FACE,{"derivedFrom":[makeQuery(id+"F1.opExtrude","CAP_FACE",FACE,{"disambiguationData":[OSD([sQuery(id+"F0.wireOp",EDGE,"E0"),subQ0])],"isStart":false}),makeQuery(id+"F2.opExtrude","CAP_FACE",FACE,{"disambiguationData":[OSD([subQ0,sQuery(id+"F0.wireOp",EDGE,"E3.bottom"),sQuery(id+"F0.wireOp",EDGE,"E3.top"),sQuery(id+"F0.wireOp",EDGE,"E3.left"),sQuery(id+"F0.wireOp",EDGE,"E3.right")])],"isStart":false})]});}
            fillet(context, id + "F61", {"entities" : qUnion([Q0, Q1, Q2, Q3, Q4, Q5, Q6]), "radius" : 1 * mm, "tangentPropagation" : true, "allowEdgeOverflow" : false});
        }
        {
            var Q0;
            Q0=makeQuery(id+"F46.opPattern","COPY",BODY,{"derivedFrom":makeQuery(id+"F1.opExtrude","SWEPT_BODY",BODY,{"disambiguationData":[OSD([sQuery(id+"F0.wireOp",EDGE,"E0"),sQuery(id+"F0.wireOp",EDGE,"E2")])]}),"instanceName":"1"});
            var Q1;
            Q1=makeQuery(id+"F1.opExtrude","SWEPT_BODY",BODY,{"disambiguationData":[OSD([sQuery(id+"F0.wireOp",EDGE,"E0"),sQuery(id+"F0.wireOp",EDGE,"E2")])]});
            transform(context, id + "F62", {"entities" : qUnion([Q0, Q1]), "transformType" : TransformType.TRANSLATION_3D, "dx" : 0 * mm, "dy" : 0.8 * mm, "dz" : 0 * mm, "makeCopy" : false});
        }
    });
